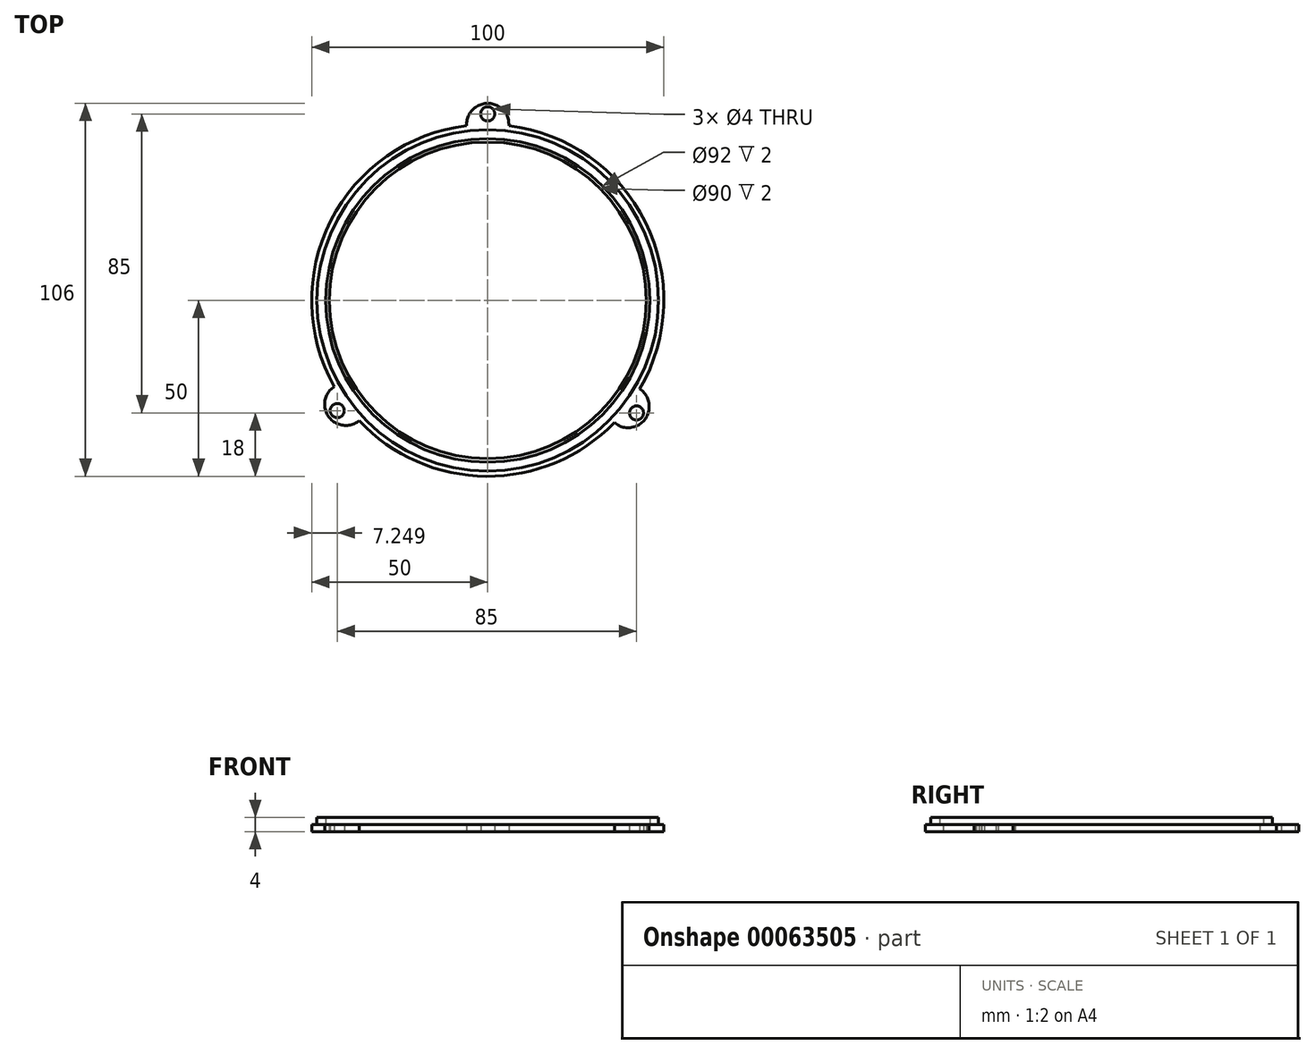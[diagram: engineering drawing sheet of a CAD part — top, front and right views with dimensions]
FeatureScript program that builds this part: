
annotation { "Feature Type Name" : "Feature", "Feature Type Description" : "" }
export const myFeature = defineFeature(function(context is Context, id is Id, definition is map)
    precondition{}
    {
        {
            var Q0;
            Q0=qCreatedBy(makeId("Top.planeOp"),FACE);
            var sketch = newSketch(context, id + "F0", { "sketchPlane" : qUnion([Q0])});
            skCircle(sketch, "E0", {"center": v(0, 0) * mm, "radius": 50 * mm});
            skCircle(sketch, "E1", {"center": v(0, 0) * mm, "radius": 45 * mm});
            skCircle(sketch, "E2", {"center": v(-42.75, -31.33) * mm, "radius": 3 * mm});
            skCircle(sketch, "E3", {"center": v(-42.75, -31.33) * mm, "radius": 2 * mm});
            skCircle(sketch, "E4", {"center": v(0, 53) * mm, "radius": 3 * mm});
            skCircle(sketch, "E5", {"center": v(0, 53) * mm, "radius": 2 * mm});
            skCircle(sketch, "E6", {"center": v(42.25, -32) * mm, "radius": 3 * mm});
            skCircle(sketch, "E7", {"center": v(42.25, -32) * mm, "radius": 2 * mm});
            skLineSegment(sketch, "E8", {"start": v(-42.75, -31.33) * mm, "end": v(0, 0) * mm});
            skLineSegment(sketch, "E9", {"start": v(42.25, -32) * mm, "end": v(0, 0) * mm});
            skLineSegment(sketch, "E10", {"start": v(0, 53) * mm, "end": v(0, 0) * mm});
            skArc(sketch, "E11", {"start": v(-43.58, -24.5) * mm, "mid": v(-45.17, -33.1) * mm, "end": v(-36.5, -34.17) * mm});
            skArc(sketch, "E12", {"start": v(35.95, -34.75) * mm, "mid": v(44.64, -33.81) * mm, "end": v(43.19, -25.2) * mm});
            skArc(sketch, "E13", {"start": v(5.99, 49.64) * mm, "mid": v(0, 56) * mm, "end": v(-5.99, 49.64) * mm});
            skCircle(sketch, "E14", {"center": v(0, 0) * mm, "radius": 48.5 * mm});
            skCircle(sketch, "E15", {"center": v(0, 0) * mm, "radius": 46 * mm});
            skSolve(sketch);
        }
        {
            var Q0;
            {var subQ0=sQuery(id+"F0.wireOp",EDGE,"E14");var subQ1=sQuery(id+"F0.wireOp",EDGE,"E8");var subQ2=makeQuery(id+"F0.imprint","INTERSECT",VERTEX,{"derivedFrom":[subQ1,subQ0]});Q0=makeQuery(id+"F0.imprint","IMPRINT",FACE,{"disambiguationData":[TD([[makeQuery(id+"F0.imprint","IMPRINT",EDGE,{"disambiguationData":[TD([[subQ2,-1.0]])],"derivedFrom":subQ1}),1.0]])]});}
            var Q1;
            {var subQ0=sQuery(id+"F0.wireOp",EDGE,"E14");var subQ1=sQuery(id+"F0.wireOp",EDGE,"E8");var subQ2=makeQuery(id+"F0.imprint","INTERSECT",VERTEX,{"derivedFrom":[subQ1,subQ0]});Q1=makeQuery(id+"F0.imprint","IMPRINT",FACE,{"disambiguationData":[TD([[makeQuery(id+"F0.imprint","IMPRINT",EDGE,{"disambiguationData":[TD([[subQ2,-1.0]])],"derivedFrom":subQ1}),-1.0]])]});}
            var Q2;
            {var subQ0=sQuery(id+"F0.wireOp",EDGE,"E14");var subQ1=sQuery(id+"F0.wireOp",EDGE,"E9");var subQ2=makeQuery(id+"F0.imprint","INTERSECT",VERTEX,{"derivedFrom":[subQ1,subQ0]});Q2=makeQuery(id+"F0.imprint","IMPRINT",FACE,{"disambiguationData":[TD([[makeQuery(id+"F0.imprint","IMPRINT",EDGE,{"disambiguationData":[TD([[subQ2,-1.0]])],"derivedFrom":subQ1}),-1.0]])]});}
            extrude(context, id + "F1", {"entities" : qUnion([Q0, Q1, Q2]), "depth" : 4 * mm});
        }
        {
            var Q0;
            {var subQ3=sQuery(id+"F0.wireOp",EDGE,"E0");var subQ8=makeQuery(id+"F0.imprint","INTERSECT",VERTEX,{"disambiguationData":[OD(0.0)],"derivedFrom":[subQ3,sQuery(id+"F0.wireOp",EDGE,"E11")]});Q0=makeQuery(id+"F0.imprint","IMPRINT",FACE,{"disambiguationData":[TD([[makeQuery(id+"F0.imprint","IMPRINT",EDGE,{"disambiguationData":[TD([[subQ8,1.0]])],"derivedFrom":subQ3}),1.0]])]});}
            var Q1;
            {var subQ0=sQuery(id+"F0.wireOp",EDGE,"E8");var subQ1=sQuery(id+"F0.wireOp",EDGE,"E1");var subQ2=makeQuery(id+"F0.imprint","INTERSECT",VERTEX,{"derivedFrom":[subQ1,subQ0]});Q1=makeQuery(id+"F0.imprint","IMPRINT",FACE,{"disambiguationData":[TD([[makeQuery(id+"F0.imprint","IMPRINT",EDGE,{"disambiguationData":[TD([[subQ2,1.0]])],"derivedFrom":subQ1}),-1.0]])]});}
            var Q2;
            {var subQ3=sQuery(id+"F0.wireOp",EDGE,"E0");var subQ8=makeQuery(id+"F0.imprint","INTERSECT",VERTEX,{"disambiguationData":[OD(1.0)],"derivedFrom":[subQ3,sQuery(id+"F0.wireOp",EDGE,"E11")]});Q2=makeQuery(id+"F0.imprint","IMPRINT",FACE,{"disambiguationData":[TD([[makeQuery(id+"F0.imprint","IMPRINT",EDGE,{"disambiguationData":[TD([[subQ8,-1.0]])],"derivedFrom":subQ3}),1.0]])]});}
            var Q3;
            {var subQ0=sQuery(id+"F0.wireOp",EDGE,"E8");var subQ1=sQuery(id+"F0.wireOp",EDGE,"E1");var subQ2=makeQuery(id+"F0.imprint","INTERSECT",VERTEX,{"derivedFrom":[subQ1,subQ0]});Q3=makeQuery(id+"F0.imprint","IMPRINT",FACE,{"disambiguationData":[TD([[makeQuery(id+"F0.imprint","IMPRINT",EDGE,{"disambiguationData":[TD([[subQ2,-1.0]])],"derivedFrom":subQ1}),-1.0]])]});}
            var Q4;
            {var subQ0=sQuery(id+"F0.wireOp",EDGE,"E11");var subQ1=sQuery(id+"F0.wireOp",EDGE,"E0");var subQ2=makeQuery(id+"F0.imprint","INTERSECT",VERTEX,{"disambiguationData":[OD(1.0)],"derivedFrom":[subQ1,subQ0]});Q4=makeQuery(id+"F0.imprint","IMPRINT",FACE,{"disambiguationData":[TD([[makeQuery(id+"F0.imprint","IMPRINT",EDGE,{"disambiguationData":[TD([[subQ2,1.0]])],"derivedFrom":subQ0}),1.0]])]});}
            var Q5;
            Q5=makeQuery(id+"F0.imprint","IMPRINT",FACE,{"disambiguationData":[TD([[makeQuery(id+"F0.imprint","IMPRINT",EDGE,{"derivedFrom":sQuery(id+"F0.wireOp",EDGE,"E3")}),-1.0]])]});
            var Q6;
            {var subQ0=sQuery(id+"F0.wireOp",EDGE,"E11");var subQ1=sQuery(id+"F0.wireOp",EDGE,"E0");var subQ2=makeQuery(id+"F0.imprint","INTERSECT",VERTEX,{"disambiguationData":[OD(0.0)],"derivedFrom":[subQ1,subQ0]});Q6=makeQuery(id+"F0.imprint","IMPRINT",FACE,{"disambiguationData":[TD([[makeQuery(id+"F0.imprint","IMPRINT",EDGE,{"disambiguationData":[TD([[subQ2,-1.0]])],"derivedFrom":subQ0}),1.0]])]});}
            var Q7;
            {var subQ0=sQuery(id+"F0.wireOp",EDGE,"E12");var subQ1=sQuery(id+"F0.wireOp",EDGE,"E0");var subQ2=makeQuery(id+"F0.imprint","INTERSECT",VERTEX,{"disambiguationData":[OD(0.0)],"derivedFrom":[subQ1,subQ0]});Q7=makeQuery(id+"F0.imprint","IMPRINT",FACE,{"disambiguationData":[TD([[makeQuery(id+"F0.imprint","IMPRINT",EDGE,{"disambiguationData":[TD([[subQ2,-1.0]])],"derivedFrom":subQ0}),1.0]])]});}
            var Q8;
            {var subQ0=sQuery(id+"F0.wireOp",EDGE,"E12");var subQ1=sQuery(id+"F0.wireOp",EDGE,"E0");var subQ2=makeQuery(id+"F0.imprint","INTERSECT",VERTEX,{"disambiguationData":[OD(1.0)],"derivedFrom":[subQ1,subQ0]});Q8=makeQuery(id+"F0.imprint","IMPRINT",FACE,{"disambiguationData":[TD([[makeQuery(id+"F0.imprint","IMPRINT",EDGE,{"disambiguationData":[TD([[subQ2,1.0]])],"derivedFrom":subQ0}),1.0]])]});}
            var Q9;
            Q9=makeQuery(id+"F0.imprint","IMPRINT",FACE,{"disambiguationData":[TD([[makeQuery(id+"F0.imprint","IMPRINT",EDGE,{"derivedFrom":sQuery(id+"F0.wireOp",EDGE,"E7")}),-1.0]])]});
            var Q10;
            {var subQ3=sQuery(id+"F0.wireOp",EDGE,"E0");var subQ5=makeQuery(id+"F0.imprint","INTERSECT",VERTEX,{"disambiguationData":[OD(1.0)],"derivedFrom":[subQ3,sQuery(id+"F0.wireOp",EDGE,"E12")]});Q10=makeQuery(id+"F0.imprint","IMPRINT",FACE,{"disambiguationData":[TD([[makeQuery(id+"F0.imprint","IMPRINT",EDGE,{"disambiguationData":[TD([[subQ5,-1.0]])],"derivedFrom":subQ3}),1.0]])]});}
            var Q11;
            {var subQ0=sQuery(id+"F0.wireOp",EDGE,"E10");var subQ1=sQuery(id+"F0.wireOp",EDGE,"E1");var subQ2=makeQuery(id+"F0.imprint","INTERSECT",VERTEX,{"derivedFrom":[subQ1,subQ0]});Q11=makeQuery(id+"F0.imprint","IMPRINT",FACE,{"disambiguationData":[TD([[makeQuery(id+"F0.imprint","IMPRINT",EDGE,{"disambiguationData":[TD([[subQ2,1.0]])],"derivedFrom":subQ1}),-1.0]])]});}
            var Q12;
            Q12=makeQuery(id+"F0.imprint","IMPRINT",FACE,{"disambiguationData":[TD([[makeQuery(id+"F0.imprint","IMPRINT",EDGE,{"derivedFrom":sQuery(id+"F0.wireOp",EDGE,"E5")}),-1.0]])]});
            var Q13;
            {var subQ0=sQuery(id+"F0.wireOp",EDGE,"E13");var subQ1=sQuery(id+"F0.wireOp",EDGE,"E0");var subQ2=makeQuery(id+"F0.imprint","INTERSECT",VERTEX,{"disambiguationData":[OD(0.0)],"derivedFrom":[subQ1,subQ0]});Q13=makeQuery(id+"F0.imprint","IMPRINT",FACE,{"disambiguationData":[TD([[makeQuery(id+"F0.imprint","IMPRINT",EDGE,{"disambiguationData":[TD([[subQ2,-1.0]])],"derivedFrom":subQ0}),1.0]])]});}
            var Q14;
            {var subQ0=sQuery(id+"F0.wireOp",EDGE,"E13");var subQ1=sQuery(id+"F0.wireOp",EDGE,"E0");var subQ2=makeQuery(id+"F0.imprint","INTERSECT",VERTEX,{"disambiguationData":[OD(1.0)],"derivedFrom":[subQ1,subQ0]});Q14=makeQuery(id+"F0.imprint","IMPRINT",FACE,{"disambiguationData":[TD([[makeQuery(id+"F0.imprint","IMPRINT",EDGE,{"disambiguationData":[TD([[subQ2,1.0]])],"derivedFrom":subQ0}),1.0]])]});}
            extrude(context, id + "F2", {"entities" : qUnion([Q0, Q1, Q2, Q3, Q4, Q5, Q6, Q7, Q8, Q9, Q10, Q11, Q12, Q13, Q14]), "operationType" : NewBodyOperationType.ADD, "depth" : 2 * mm});
        }
    });
